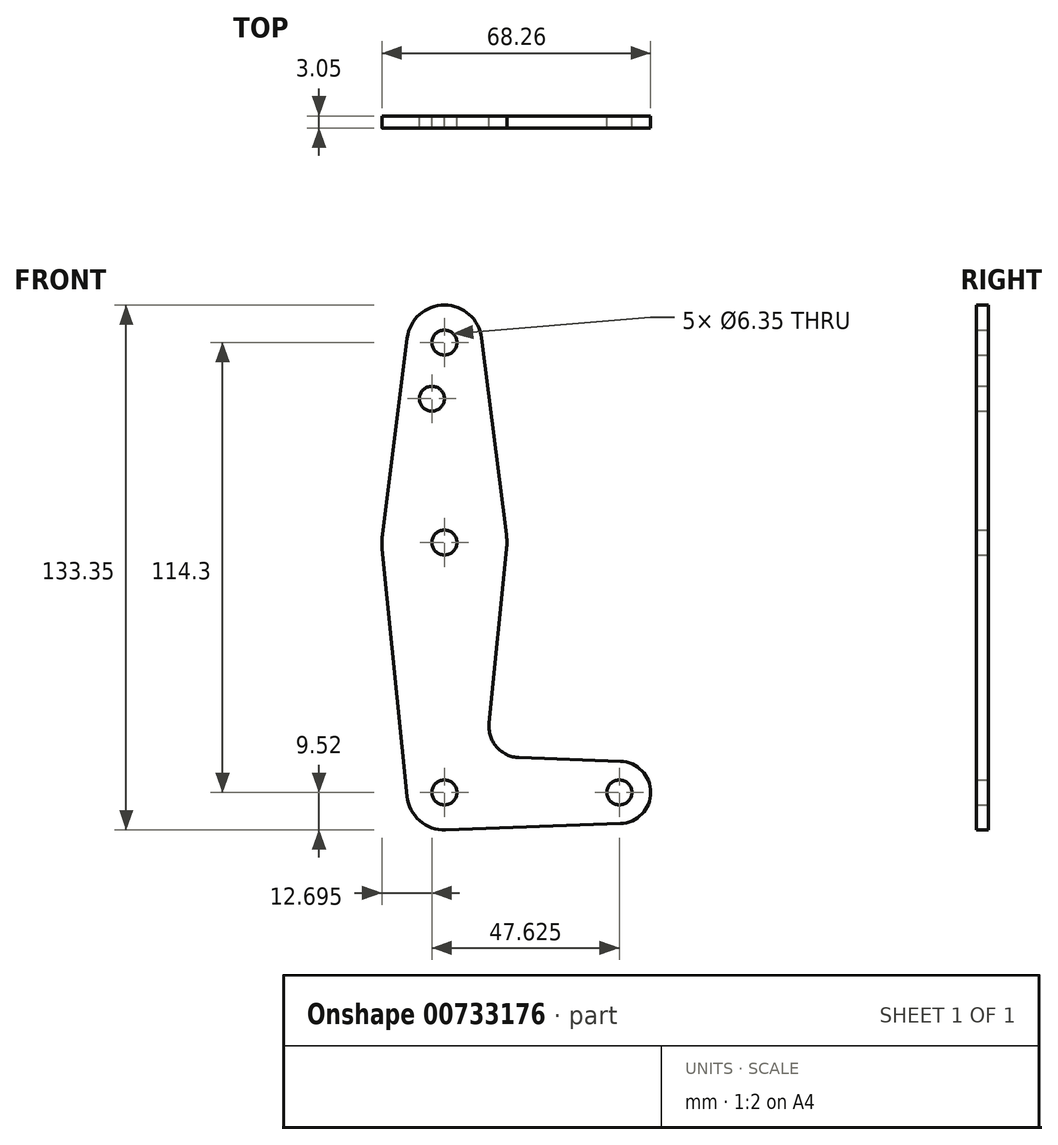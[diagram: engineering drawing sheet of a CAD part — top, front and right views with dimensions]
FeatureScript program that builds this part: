
annotation { "Feature Type Name" : "Feature", "Feature Type Description" : "" }
export const myFeature = defineFeature(function(context is Context, id is Id, definition is map)
    precondition{}
    {
        {
            var Q0;
            Q0=qCreatedBy(makeId("Front.planeOp"),FACE);
            var sketch = newSketch(context, id + "F0", { "sketchPlane" : qUnion([Q0])});
            skCircle(sketch, "E0", {"center": v(0, 0) * mm, "radius": 9.53 * mm});
            skCircle(sketch, "E1", {"center": v(44.45, 0) * mm, "radius": 7.94 * mm});
            skCircle(sketch, "E2", {"center": v(0, 63.5) * mm, "radius": 15.88 * mm});
            skCircle(sketch, "E3", {"center": v(0, 114.3) * mm, "radius": 9.53 * mm});
            skLineSegment(sketch, "E4", {"start": v(0, 114.3) * mm, "end": v(0, 0) * mm, "construction": true});
            skLineSegment(sketch, "E5", {"start": v(0, 0) * mm, "end": v(44.45, 0) * mm, "construction": true});
            skLineSegment(sketch, "E6", {"start": v(-9.45, 115.5) * mm, "end": v(-15.75, 65.48) * mm});
            skLineSegment(sketch, "E7", {"start": v(9.45, 115.5) * mm, "end": v(15.75, 65.48) * mm});
            skLineSegment(sketch, "E8", {"start": v(15.8, 61.91) * mm, "end": v(11.34, 17.6) * mm});
            skLineSegment(sketch, "E9", {"start": v(-15.8, 61.91) * mm, "end": v(-9.48, -0.95) * mm});
            skLineSegment(sketch, "E10", {"start": v(18.97, 8.85) * mm, "end": v(44.73, 7.93) * mm});
            skLineSegment(sketch, "E11", {"start": v(0.34, -9.52) * mm, "end": v(44.73, -7.93) * mm});
            skCircle(sketch, "E12", {"center": v(0, 114.3) * mm, "radius": 3.18 * mm});
            skCircle(sketch, "E13", {"center": v(0, 63.5) * mm, "radius": 3.18 * mm});
            skCircle(sketch, "E14", {"center": v(0, 0) * mm, "radius": 3.18 * mm});
            skCircle(sketch, "E15", {"center": v(44.45, 0) * mm, "radius": 3.18 * mm});
            skCircle(sketch, "E16", {"center": v(-3.17, 100.03) * mm, "radius": 3.18 * mm});
            skArc(sketch, "E17.filletArc", {"start": v(11.34, 17.6) * mm, "mid": v(13.26, 11.57) * mm, "end": v(18.97, 8.85) * mm});
            skSolve(sketch);
        }
        {
            var Q0;
            Q0=makeQuery(id+"F0.imprint","IMPRINT",FACE,{"disambiguationData":[TD([[makeQuery(id+"F0.imprint","IMPRINT",EDGE,{"derivedFrom":sQuery(id+"F0.wireOp",EDGE,"E12")}),-1.0]])]});
            var Q1;
            {var subQ1=sQuery(id+"F0.wireOp",EDGE,"E6");Q1=makeQuery(id+"F0.imprint","IMPRINT",FACE,{"disambiguationData":[TD([[makeQuery(id+"F0.imprint","IMPRINT",EDGE,{"derivedFrom":subQ1}),1.0]])]});}
            var Q2;
            Q2=makeQuery(id+"F0.imprint","IMPRINT",FACE,{"disambiguationData":[TD([[makeQuery(id+"F0.imprint","IMPRINT",EDGE,{"derivedFrom":sQuery(id+"F0.wireOp",EDGE,"E13")}),-1.0]])]});
            var Q3;
            {var subQ0=sQuery(id+"F0.wireOp",EDGE,"E8");Q3=makeQuery(id+"F0.imprint","IMPRINT",FACE,{"disambiguationData":[TD([[makeQuery(id+"F0.imprint","IMPRINT",EDGE,{"derivedFrom":subQ0}),-1.0]])]});}
            var Q4;
            Q4=makeQuery(id+"F0.imprint","IMPRINT",FACE,{"disambiguationData":[TD([[makeQuery(id+"F0.imprint","IMPRINT",EDGE,{"derivedFrom":sQuery(id+"F0.wireOp",EDGE,"E15")}),-1.0]])]});
            var Q5;
            Q5=makeQuery(id+"F0.imprint","IMPRINT",FACE,{"disambiguationData":[TD([[makeQuery(id+"F0.imprint","IMPRINT",EDGE,{"derivedFrom":sQuery(id+"F0.wireOp",EDGE,"E14")}),-1.0]])]});
            extrude(context, id + "F1", {"entities" : qUnion([Q0, Q1, Q2, Q3, Q4, Q5]), "depth" : 3.05 * mm, "offsetDistance" : 25.4 * mm});
        }
    });
